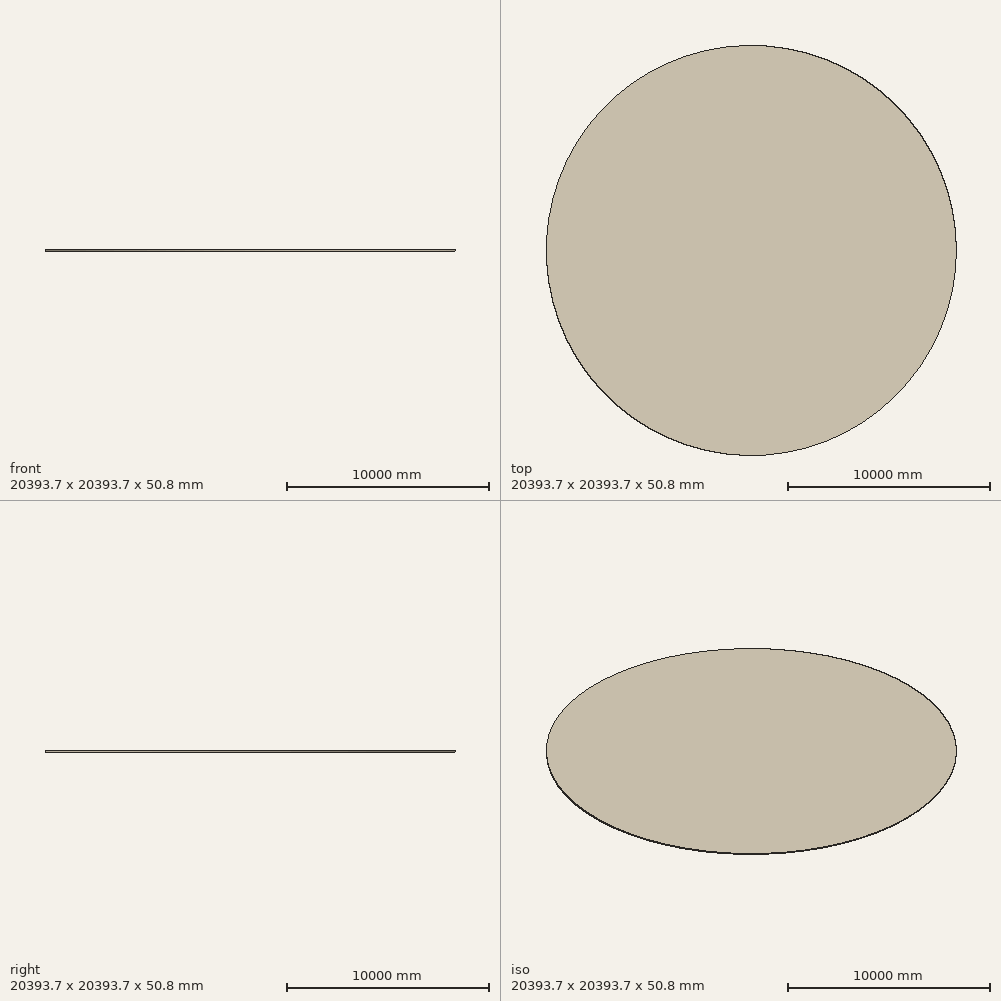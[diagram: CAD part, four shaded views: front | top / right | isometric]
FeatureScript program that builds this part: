
annotation { "Feature Type Name" : "Feature", "Feature Type Description" : "" }
export const myFeature = defineFeature(function(context is Context, id is Id, definition is map)
    precondition{}
    {
        {
            var Q0;
            Q0=qCreatedBy(makeId("Top.planeOp"),FACE);
            var sketch = newSketch(context, id + "F0", { "sketchPlane" : qUnion([Q0])});
            skCircle(sketch, "E0", {"center": v(0, 0) * mm, "radius": 36.86 * mm});
            skCircle(sketch, "E1", {"center": v(0, 0) * mm, "radius": 22.75 * mm});
            skCircle(sketch, "E2.0", {"center": v(0, 0) * mm, "radius": 10196.86 * mm});
            skSolve(sketch);
        }
        {
            var Q0;
            Q0=makeQuery(id+"F0.imprint","IMPRINT",FACE,{"disambiguationData":[TD([[makeQuery(id+"F0.imprint","IMPRINT",EDGE,{"derivedFrom":sQuery(id+"F0.wireOp",EDGE,"E0")}),1.0]])]});
            var Q1;
            Q1 = qSketchRegion(id + "F0", true);
            extrude(context, id + "F1", {"entities" : qUnion([Q0, Q1]), "depth" : 25.4 * mm, "offsetDistance" : 25.4 * mm});
        }
        {
            var Q0;
            Q0=makeQuery(id+"F0.imprint","IMPRINT",FACE,{"disambiguationData":[TD([[makeQuery(id+"F0.imprint","IMPRINT",EDGE,{"derivedFrom":sQuery(id+"F0.wireOp",EDGE,"E1")}),1.0]])]});
            extrude(context, id + "F2", {"entities" : qUnion([Q0]), "operationType" : NewBodyOperationType.ADD, "depth" : 25.4 * mm, "offsetDistance" : 25.4 * mm});
        }
        {
            var Q0;
            {var subQ0=sQuery(id+"F0.wireOp",EDGE,"E1");Q0=makeQuery(id+"F2.boolean.opBoolean","MERGE",FACE,{"derivedFrom":[makeQuery(id+"F1.opExtrude","CAP_FACE",FACE,{"disambiguationData":[OSD([sQuery(id+"F0.wireOp",EDGE,"E0"),subQ0])],"isStart":false}),makeQuery(id+"F2.opExtrude","CAP_FACE",FACE,{"disambiguationData":[OSD([subQ0])],"isStart":false})]});}
            var Q1;
            Q1=makeQuery(id+"F0.imprint","IMPRINT",FACE,{"disambiguationData":[TD([[makeQuery(id+"F0.imprint","IMPRINT",EDGE,{"derivedFrom":sQuery(id+"F0.wireOp",EDGE,"E1")}),1.0]])]});
            extrude(context, id + "F3", {"entities" : qUnion([Q0, Q1]), "operationType" : NewBodyOperationType.ADD, "depth" : 25.4 * mm, "offsetDistance" : 25.4 * mm});
        }
    });
